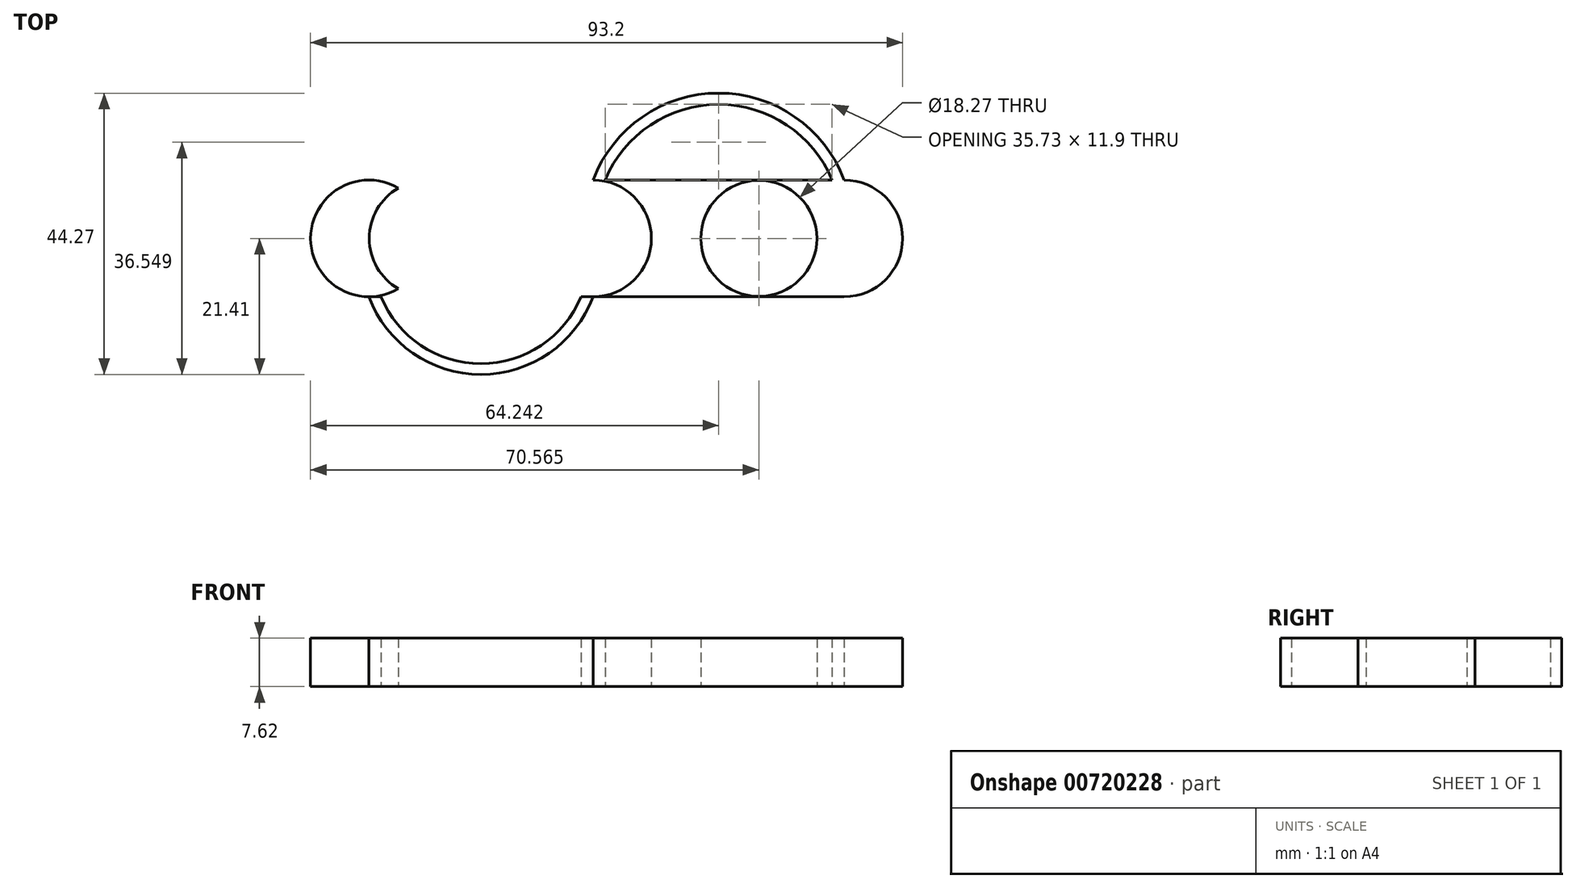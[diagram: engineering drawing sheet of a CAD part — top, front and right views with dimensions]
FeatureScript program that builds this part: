
annotation { "Feature Type Name" : "Feature", "Feature Type Description" : "" }
export const myFeature = defineFeature(function(context is Context, id is Id, definition is map)
    precondition{}
    {
        {
            var Q0;
            Q0=qCreatedBy(makeId("Top.planeOp"),FACE);
            var sketch = newSketch(context, id + "F0", { "sketchPlane" : qUnion([Q0])});
            skPoint(sketch, "E0.center", {"position": v(0, 0) * mm});
            skCircle(sketch, "E1", {"center": v(0, 0) * mm, "radius": 9.19 * mm});
            skCircle(sketch, "E2", {"center": v(-35.28, 0) * mm, "radius": 9.19 * mm});
            skCircle(sketch, "E3", {"center": v(39.54, 0) * mm, "radius": 9.19 * mm});
            skLineSegment(sketch, "E4", {"start": v(-35.28, 9.19) * mm, "end": v(39.54, 9.19) * mm});
            skLineSegment(sketch, "E5", {"start": v(-35.28, -9.19) * mm, "end": v(39.54, -9.19) * mm});
            skArc(sketch, "E6", {"start": v(39.54, 9.19) * mm, "mid": v(19.77, 22.86) * mm, "end": v(0, 9.19) * mm});
            skArc(sketch, "E7", {"start": v(-35.28, -9.19) * mm, "mid": v(-17.64, -21.41) * mm, "end": v(0, -9.19) * mm});
            skLineSegment(sketch, "E8", {"start": v(-35.28, -9.19) * mm, "end": v(-33.38, -9.19) * mm});
            skLineSegment(sketch, "E9", {"start": v(0, -9.19) * mm, "end": v(-1.9, -9.19) * mm});
            skArc(sketch, "E10", {"start": v(-33.38, -9.19) * mm, "mid": v(-17.64, -19.71) * mm, "end": v(-1.9, -9.19) * mm});
            skArc(sketch, "E11.MirrorCS", {"start": v(37.7, 9.04) * mm, "mid": v(19.85, 21.1) * mm, "end": v(1.9, 9.19) * mm});
            skCircle(sketch, "E12", {"center": v(-26.1, 0) * mm, "radius": 9.13 * mm});
            skCircle(sketch, "E13.MirrorC", {"center": v(26.1, 0) * mm, "radius": 9.13 * mm});
            skSolve(sketch);
        }
        {
            var Q0;
            {var subQ0=sQuery(id+"F0.wireOp",EDGE,"E2");var subQ1=makeQuery(id+"F0.imprint","INTERSECT",VERTEX,{"derivedFrom":[subQ0,sQuery(id+"F0.wireOp",EDGE,"E4")]});Q0=makeQuery(id+"F0.imprint","IMPRINT",FACE,{"disambiguationData":[TD([[makeQuery(id+"F0.imprint","IMPRINT",EDGE,{"disambiguationData":[TD([[subQ1,1.0]])],"derivedFrom":subQ0}),1.0]])]});}
            var Q1;
            {var subQ0=sQuery(id+"F0.wireOp",EDGE,"E3");var subQ4=makeQuery(id+"F0.imprint","INTERSECT",VERTEX,{"derivedFrom":[subQ0,sQuery(id+"F0.wireOp",EDGE,"E5")]});Q1=makeQuery(id+"F0.imprint","IMPRINT",FACE,{"disambiguationData":[TD([[makeQuery(id+"F0.imprint","IMPRINT",EDGE,{"disambiguationData":[TD([[subQ4,1.0]])],"derivedFrom":subQ0}),1.0]])]});}
            var Q2;
            {var subQ0=sQuery(id+"F0.wireOp",EDGE,"E6");Q2=makeQuery(id+"F0.imprint","IMPRINT",FACE,{"disambiguationData":[TD([[makeQuery(id+"F0.imprint","IMPRINT",EDGE,{"derivedFrom":subQ0}),1.0]])]});}
            var Q3;
            {var subQ1=sQuery(id+"F0.wireOp",EDGE,"E7");Q3=makeQuery(id+"F0.imprint","IMPRINT",FACE,{"disambiguationData":[TD([[makeQuery(id+"F0.imprint","IMPRINT",EDGE,{"derivedFrom":subQ1}),1.0]])]});}
            var Q4;
            {var subQ8=sQuery(id+"F0.wireOp",EDGE,"E8");Q4=makeQuery(id+"F0.imprint","IMPRINT",FACE,{"disambiguationData":[TD([[makeQuery(id+"F0.imprint","IMPRINT",EDGE,{"derivedFrom":subQ8}),1.0]])]});}
            var Q5;
            {var subQ0=sQuery(id+"F0.wireOp",EDGE,"E5");var subQ1=sQuery(id+"F0.wireOp",EDGE,"E3");var subQ2=makeQuery(id+"F0.imprint","INTERSECT",VERTEX,{"derivedFrom":[subQ1,subQ0]});Q5=makeQuery(id+"F0.imprint","IMPRINT",FACE,{"disambiguationData":[TD([[makeQuery(id+"F0.imprint","IMPRINT",EDGE,{"disambiguationData":[TD([[subQ2,1.0]])],"derivedFrom":subQ1}),-1.0]])]});}
            extrude(context, id + "F1", {"entities" : qUnion([Q0, Q1, Q2, Q3, Q4, Q5]), "depth" : 7.62 * mm, "offsetDistance" : 25.4 * mm});
        }
    });
